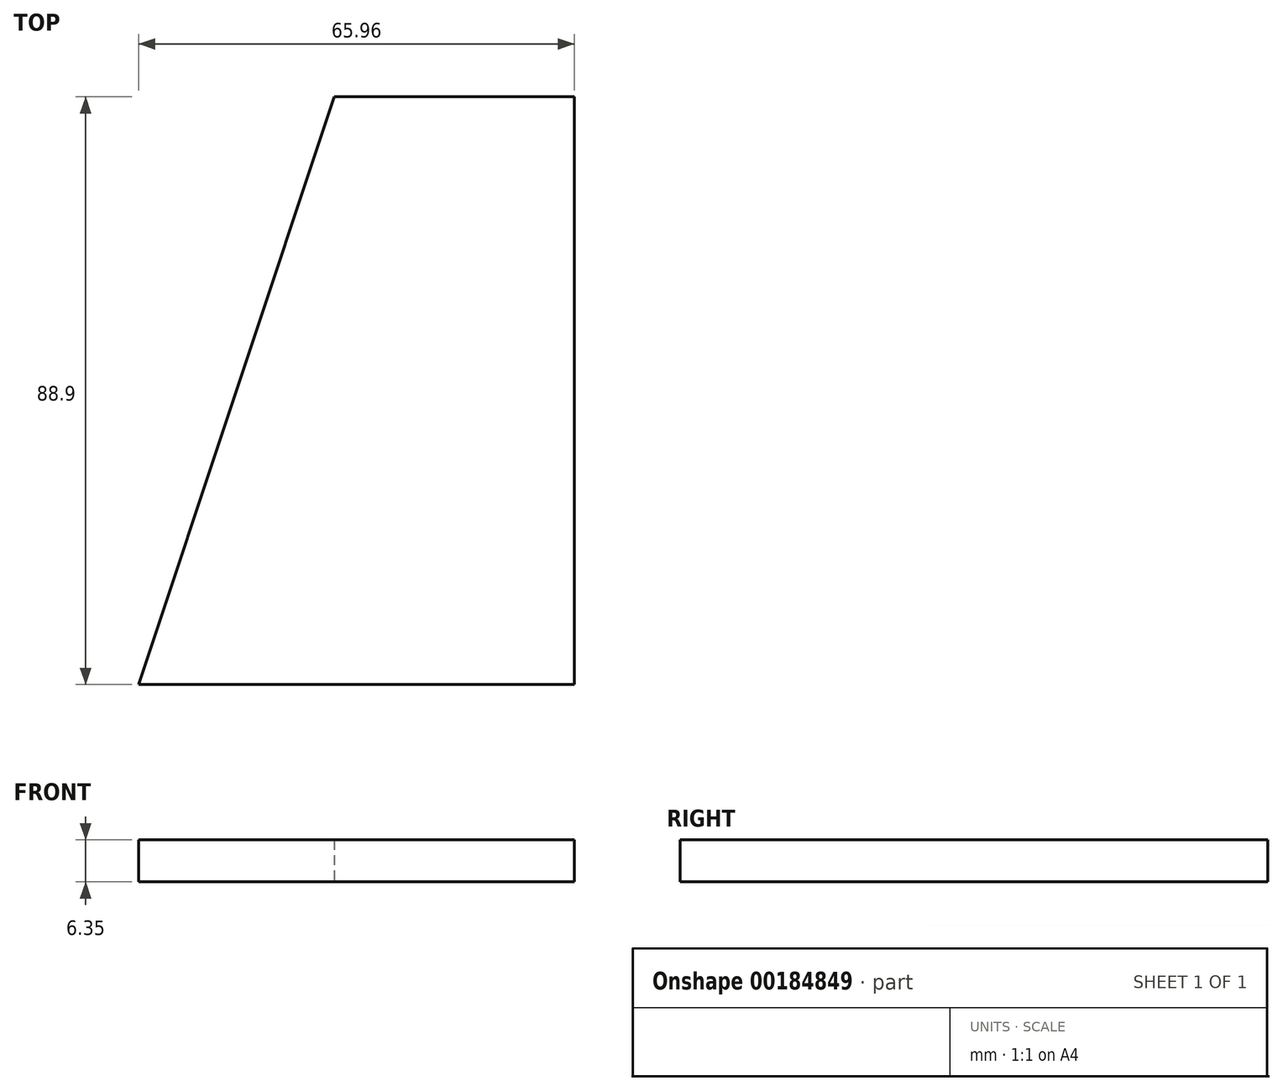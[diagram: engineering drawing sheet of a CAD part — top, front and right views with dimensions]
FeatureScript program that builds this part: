
annotation { "Feature Type Name" : "Feature", "Feature Type Description" : "" }
export const myFeature = defineFeature(function(context is Context, id is Id, definition is map)
    precondition{}
    {
        {
            var Q0;
            Q0=qCreatedBy(makeId("Top.planeOp"),FACE);
            var sketch = newSketch(context, id + "F0", { "sketchPlane" : qUnion([Q0])});
            skLineSegment(sketch, "E0", {"start": v(-5.38, 48.26) * mm, "end": v(30.95, 48.26) * mm});
            skLineSegment(sketch, "E1", {"start": v(30.95, 48.26) * mm, "end": v(30.95, -40.64) * mm});
            skLineSegment(sketch, "E2", {"start": v(-35.01, -40.64) * mm, "end": v(30.95, -40.64) * mm});
            skLineSegment(sketch, "E3", {"start": v(-35.01, -40.64) * mm, "end": v(-5.38, 48.26) * mm});
            skSolve(sketch);
        }
        {
            var Q0;
            Q0 = qSketchRegion(id + "F0", true);
            extrude(context, id + "F1", {"entities" : qUnion([Q0]), "depth" : 6.35 * mm});
        }
    });
